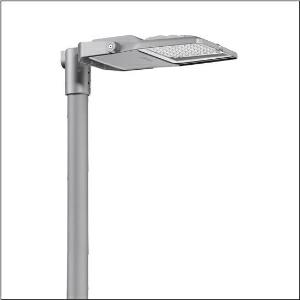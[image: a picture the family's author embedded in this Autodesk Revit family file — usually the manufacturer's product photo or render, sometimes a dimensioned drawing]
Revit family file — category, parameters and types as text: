
# Revit family: floodlight_fl_21_iq_mini___pl43_5xa7772d4a3a_0702
name_source: partatom
category: Lighting Fixtures
units: mm (PartAtom-declared; Revit-internal decimal feet)

## family parameters
Cut with Voids When Loaded = No
Host = Face
Light Source = No
Part Type = Normal
Room Calculation Point = No
Round Connector Dimension = Use Diameter
Shared = No

## types (1)
- --- (1 x LED, 19090 lm, 143 W, 4000K)
    Apparent Load = 143 VA
    CIE Flux Codes = 27 78 99 100 100
    Color Rendering = 70
    Color Temperature = 4000K
    Default Elevation = 1800 mm
    Description = Floodlight FL 21 iQ mini, floodlight, primary light control with lens, of PMMA, primary optical cover: protective disc, of toughened safety glass, transparent, light distribution: PL43, light emission: direct distribution, installation type: surface-mounted, lamps: LED, High Power LED, rated values: 19.090lm | 143W | 133,5lm/W (begin service life); end service life: 19.090lm | 151,6W; at 50% lumin. flux: 9.545lm | 60,8W | 157lm/W, colour temperature: 4000K, colour rendering: CRI > 70, light colour: 740, light setting 1 begin service life: 100% | 19.090lm | 143W | 133,5lm/W | 4.000K, light setting 1 end service life: 151,6W, further light settings possible, control: Street-Remote, Auto-Match, Temp-Guard, Night-Set, Smart-Wire, Desk-Remote (wireless, voltage-free reading and setting of iQ features in the workshop via application-optimized NFC function/RFID function), optimised constant luminous flux control (CLO 2.0), pre-setting: linear dimming characteristic, with terminal, 6-pole, mains connection: 220..240V, AC, 50/60Hz, luminaire housing, of diecast aluminium, powder-coated, SITECO metallic grey (DB 702S), corrosivity category C5 mid according to DIN EN ISO 12944suitable for swimming poolschlorine-resistant, sealing non-destructively replaceable, please order mast flange separately, mast bracket, of steel, galvanised, powder-coated, protection rating (complete): IP66, insulation class (complete): insulation class II (safety insulation), certification: CE, ENEC, VDE, protection symbol: D, impact resistance: IK08, permissible operating ambient temperature: -40..+40°C, permissible operating ambient temperature for outdoor applications: -40..+50°C, standard: DIN EN 12944, LABS conformity tested according to VDMA 24364:2018-05, packaging unit: 1 piece

Light Distribution: PL43
    Height = 70 mm
    Lamp = 1 x LED
    Lamp Light Flux = 19090 lm
    Lamp Power = 143 W
    Lamp count = 1
    Length = 485 mm
    Luminous efficacy = 133 lm/W
    Manufacturer = Siteco
    ModVariant = No
    Model = 5XA7772D4A3A
    Mounting Place = Pole
    Mounting Type = Pole annexe
    Number of Poles = 1
    OnlyDefault = Yes
    Power Factor = 1
    Product Name = Floodlight FL 21 iQ mini | PL43
    Product group = floodlight | pylon annexe
    ProductGroupID = 6201
    Protection Class = Protection class II
    Protection Degree = IP 66
    RLX_Detail_Level = 1
    RLX_Emergency_Light_Flux = 0 lm
    RLX_Emergency_Type = 0
    RLX_Emergency_Type_DB = No
    RlxData = <blob elided: 101781 chars, md5=6ab62854>
    Socket = socket
    Standby Power = 0 W
    System Light Flux = 19090 lm
    System Power = 143 W
    Type Comments = factory setting: luminous flux: 100 % | dim-lin: 254 | 730 mA
    Type Image = l_1007125.jpg
    URL = http://relux.com
    VarID = @adj_162491
    Voltage = 0 V
    Weight = 0.00 kg
    Width = 337 mm

## geometry (parser evidence)
native form markers: Blend x4, Sweep x12
no freeform markers — native parametric forms only
